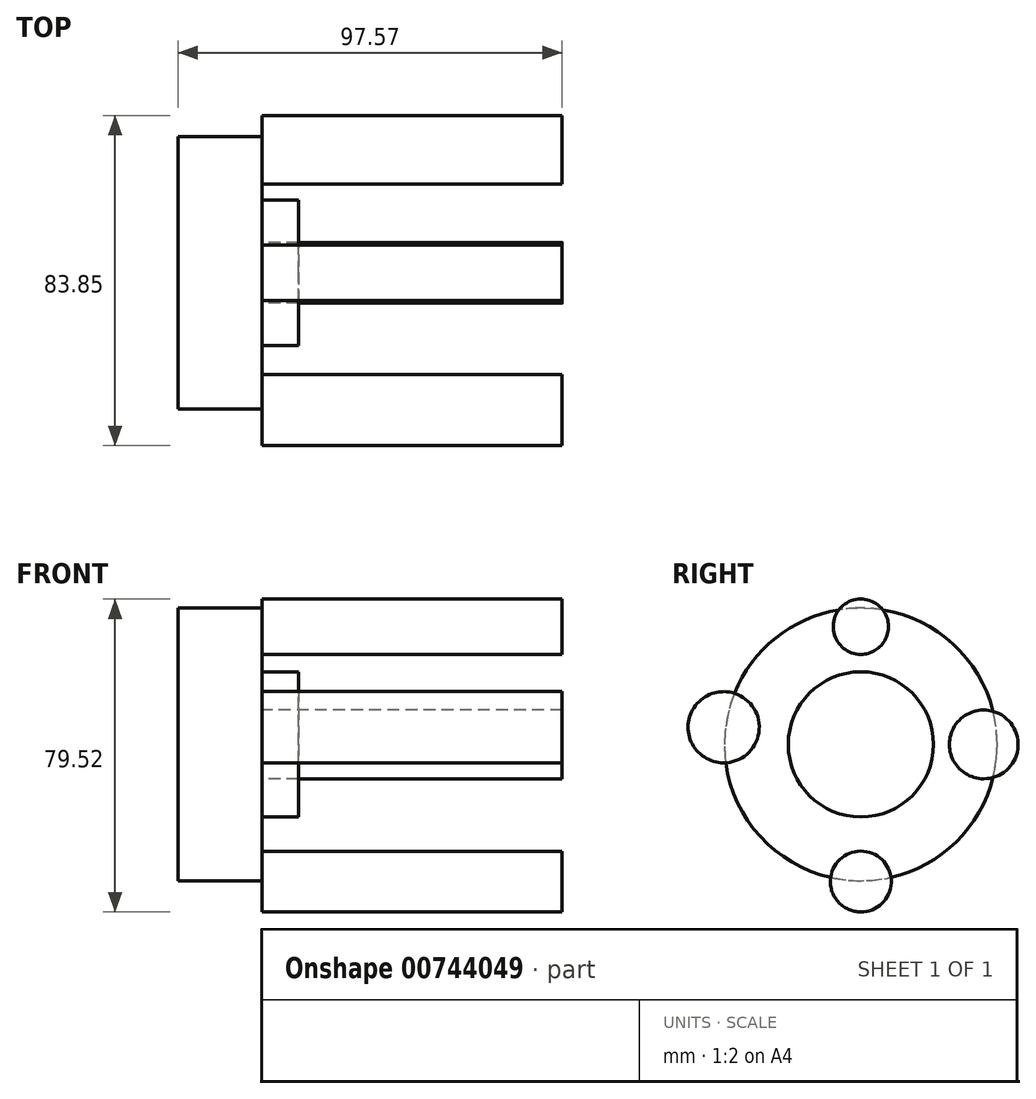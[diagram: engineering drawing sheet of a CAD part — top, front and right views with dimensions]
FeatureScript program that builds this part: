
annotation { "Feature Type Name" : "Feature", "Feature Type Description" : "" }
export const myFeature = defineFeature(function(context is Context, id is Id, definition is map)
    precondition{}
    {
        {
            var Q0;
            Q0=qCreatedBy(makeId("Front.planeOp"),FACE);
            var sketch = newSketch(context, id + "F0", { "sketchPlane" : qUnion([Q0])});
            skLineSegment(sketch, "E0", {"start": v(-21.37, 34.64) * mm, "end": v(-21.37, 0) * mm});
            skLineSegment(sketch, "E1", {"start": v(-21.37, 34.64) * mm, "end": v(0, 34.64) * mm});
            skLineSegment(sketch, "E2", {"start": v(-21.37, 0) * mm, "end": v(9.22, 0) * mm});
            skLineSegment(sketch, "E3", {"start": v(0, 34.64) * mm, "end": v(0, 18.44) * mm});
            skLineSegment(sketch, "E4", {"start": v(0, 18.44) * mm, "end": v(9.22, 18.44) * mm});
            skLineSegment(sketch, "E5", {"start": v(9.22, 18.44) * mm, "end": v(9.22, 0) * mm});
            skSolve(sketch);
        }
        {
            var Q0;
            Q0=makeQuery(id+"F0.imprint","IMPRINT",FACE,{"disambiguationData":[TD([[makeQuery(id+"F0.imprint","IMPRINT",EDGE,{"derivedFrom":sQuery(id+"F0.wireOp",EDGE,"E0")}),1.0]])]});
            var Q1;
            Q1=sQuery(id+"F0.wireOp",EDGE,"E2");
            revolve(context, id + "F1", {"surfaceOperationType" : NewSurfaceOperationType.NEW, "entities" : qUnion([Q0]), "axis" : qUnion([Q1]), "revolveType" : RevolveType.FULL});
        }
        {
            var Q0;
            Q0=qCreatedBy(makeId("Right.planeOp"),FACE);
            var sketch = newSketch(context, id + "F2", { "sketchPlane" : qUnion([Q0])});
            skCircle(sketch, "E6", {"center": v(0, 29.91) * mm, "radius": 7.03 * mm});
            skCircle(sketch, "E7", {"center": v(-34.85, 4.36) * mm, "radius": 9.04 * mm});
            skCircle(sketch, "E8", {"center": v(31.22, 0) * mm, "radius": 8.74 * mm});
            skCircle(sketch, "E9", {"center": v(0, -34.85) * mm, "radius": 7.73 * mm});
            skSolve(sketch);
        }
        {
            var Q0;
            Q0=makeQuery(id+"F2.imprint","IMPRINT",FACE,{"disambiguationData":[TD([[makeQuery(id+"F2.imprint","IMPRINT",EDGE,{"derivedFrom":sQuery(id+"F2.wireOp",EDGE,"E9")}),1.0]])]});
            var Q1;
            Q1=makeQuery(id+"F2.imprint","IMPRINT",FACE,{"disambiguationData":[TD([[makeQuery(id+"F2.imprint","IMPRINT",EDGE,{"derivedFrom":sQuery(id+"F2.wireOp",EDGE,"E7")}),1.0]])]});
            var Q2;
            Q2=makeQuery(id+"F2.imprint","IMPRINT",FACE,{"disambiguationData":[TD([[makeQuery(id+"F2.imprint","IMPRINT",EDGE,{"derivedFrom":sQuery(id+"F2.wireOp",EDGE,"E6")}),1.0]])]});
            var Q3;
            Q3=makeQuery(id+"F2.imprint","IMPRINT",FACE,{"disambiguationData":[TD([[makeQuery(id+"F2.imprint","IMPRINT",EDGE,{"derivedFrom":sQuery(id+"F2.wireOp",EDGE,"E8")}),1.0]])]});
            extrude(context, id + "F3", {"entities" : qUnion([Q0, Q1, Q2, Q3]), "operationType" : NewBodyOperationType.ADD, "depth" : 76.2 * mm, "offsetDistance" : 25.4 * mm});
        }
    });
